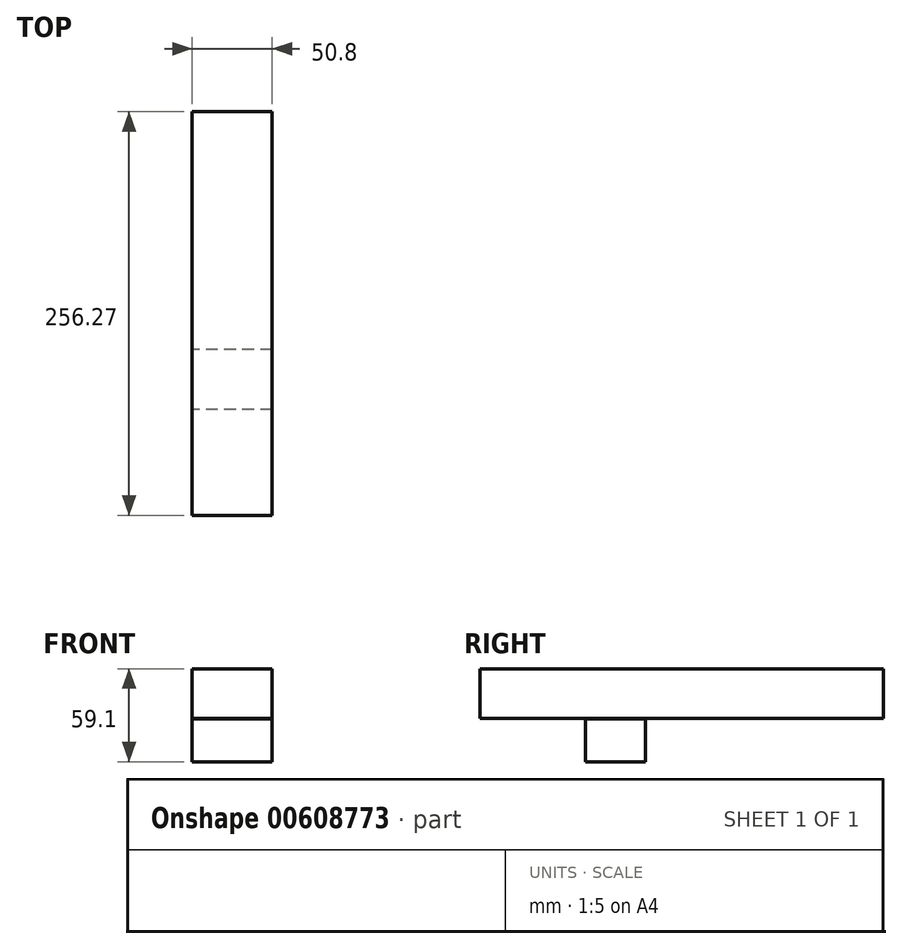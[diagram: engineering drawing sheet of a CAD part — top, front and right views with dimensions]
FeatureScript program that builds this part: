
annotation { "Feature Type Name" : "Feature", "Feature Type Description" : "" }
export const myFeature = defineFeature(function(context is Context, id is Id, definition is map)
    precondition{}
    {
        {
            var Q0;
            Q0=qCreatedBy(makeId("Right.planeOp"),FACE);
            var sketch = newSketch(context, id + "F0", { "sketchPlane" : qUnion([Q0])});
            skLineSegment(sketch, "E0.bottom", {"start": v(-65.7, 31.5) * mm, "end": v(190.57, 31.5) * mm});
            skLineSegment(sketch, "E0.top", {"start": v(-65.7, 0) * mm, "end": v(190.57, 0) * mm});
            skLineSegment(sketch, "E0.left", {"start": v(-65.7, 31.5) * mm, "end": v(-65.7, 0) * mm});
            skLineSegment(sketch, "E0.right", {"start": v(190.57, 31.5) * mm, "end": v(190.57, 0) * mm});
            skLineSegment(sketch, "E1.bottom", {"start": v(190.57, 0) * mm, "end": v(-65.7, 0) * mm});
            skLineSegment(sketch, "E1.top", {"start": v(190.57, 31.5) * mm, "end": v(-65.7, 31.5) * mm});
            skLineSegment(sketch, "E1.left", {"start": v(190.57, 0) * mm, "end": v(190.57, 31.5) * mm});
            skLineSegment(sketch, "E1.right", {"start": v(-65.7, 0) * mm, "end": v(-65.7, 31.5) * mm});
            skLineSegment(sketch, "E2.bottom", {"start": v(1.4, -0.43) * mm, "end": v(39.6, -0.43) * mm});
            skLineSegment(sketch, "E2.top", {"start": v(1.4, -27.6) * mm, "end": v(39.6, -27.6) * mm});
            skLineSegment(sketch, "E2.left", {"start": v(1.4, -0.43) * mm, "end": v(1.4, -27.6) * mm});
            skLineSegment(sketch, "E2.right", {"start": v(39.6, -0.43) * mm, "end": v(39.6, -27.6) * mm});
            skSolve(sketch);
        }
        {
            var Q0;
            Q0 = qSketchRegion(id + "F0", true);
            extrude(context, id + "F1", {"entities" : qUnion([Q0]), "depth" : 50.8 * mm, "offsetDistance" : 25.4 * mm});
        }
    });
